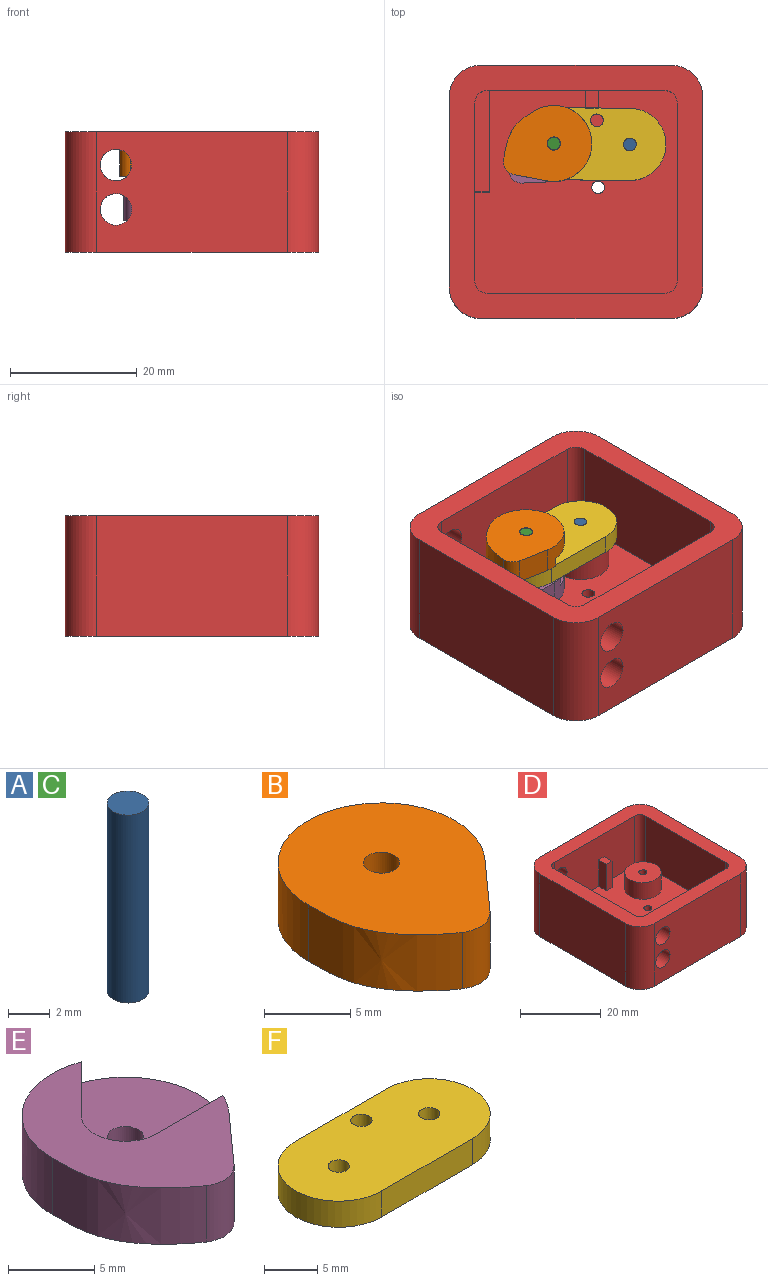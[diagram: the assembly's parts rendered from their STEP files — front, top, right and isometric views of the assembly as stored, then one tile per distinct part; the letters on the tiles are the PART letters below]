
ASSEMBLY  parts=6 mates=10
PART A: 3 faces, bbox 2x2x11 mm
  f0: cylinder r=1mm len=11mm, axis (0,0,-1), area 69.1mm2, adj f1,f2
  f1: plane 2x2mm, normal (0,0,1), area 3.1mm2, adj f0
  f2: plane 2x2mm, normal (0,0,-1), area 3.1mm2, adj f0
PART B: 11 faces, bbox 12.1x14.6x4 mm
  f0: cylinder r=6mm len=12mm, axis (0,0,-1), area 77.9mm2, adj f1,f2,f5,f6,f7,f8,f9
  f1: plane 4x3.93mm, normal (0.75,-0.67,0), area 21.1mm2, adj f0,f4,f5,f6
  f2: extruded ~8.25x4.36mm, area 39.4mm2, adj f0,f4,f5,f6
  f3: cylinder r=1.05mm len=2.5mm, axis (0,0,-1), area 16.5mm2, adj f5,f7
  f4: cylinder r=2mm len=4mm, axis (0,0,-1), area 11.5mm2, adj f1,f2,f5,f6
  f5: plane 14.59x12.11mm, normal (0,0,1), area 126.6mm2, adj f0,f1,f2,f3,f4
  f6: plane 14.59x11.54mm, normal (0,0,-1), area 78.6mm2, adj f0,f1,f2,f4,f8,f9,f10
  f7: plane 8.55x8.19mm, normal (0,0,-1), area 48mm2, adj f0,f3,f8,f9,f10
  f8: plane 5.43x1.5mm, normal (0,1,0), area 8.1mm2, adj f0,f6,f7,f10
  f9: plane 3.84x3.84mm, normal (0.71,-0.71,0), area 8.1mm2, adj f0,f6,f7,f10
  f10: cylinder r=2.55mm len=4.35mm, axis (0,0,-1), area 9mm2, adj f6,f7,f8,f9
PART C: same geometry as A
PART D: 36 faces, bbox 40x40x19 mm
  f0: plane 32x32mm, normal (0,0,1), area 911.9mm2, adj f1,f3,f14,f15,f16,f17,f18,f19
  f1: plane 28x15mm, normal (1,0,0), area 257mm2, adj f0,f2,f12,f14,f31,f35
  f2: cylinder r=2mm len=3.35mm, axis (0,0,1), area 10.5mm2, adj f1,f3,f12,f31
  f3: plane 28x15mm, normal (0,-1,0), area 365.2mm2, adj f0,f2,f12,f18,f22,f24,f25,f27
  f4: plane 30x19mm, normal (1,0,0), area 570mm2, adj f5,f11,f12,f13
  f5: cylinder r=5mm len=19mm, axis (0,0,-1), area 149.2mm2, adj f4,f6,f12,f13
  f6: plane 30x19mm, normal (0,1,0), area 530.7mm2, adj f5,f7,f12,f13,f27,f28
  f7: cylinder r=5mm len=19mm, axis (0,0,-1), area 149.2mm2, adj f6,f8,f12,f13
  f8: plane 30x19mm, normal (-1,0,0), area 570mm2, adj f7,f9,f12,f13
  f9: cylinder r=5mm len=19mm, axis (0,0,-1), area 149.2mm2, adj f8,f10,f12,f13
  f10: plane 30x19mm, normal (0,-1,0), area 530.7mm2, adj f9,f11,f12,f13,f29,f30
  f11: cylinder r=5mm len=19mm, axis (0,0,-1), area 149.2mm2, adj f4,f10,f12,f13
  f12: plane 40x40mm, normal (0,0,1), area 558mm2, adj f1,f2,f3,f4,f5,f6,f7,f8
  f13: plane 40x40mm, normal (0,0,-1), area 1572.3mm2, adj f4,f5,f6,f7,f8,f9,f10,f11
  f14: cylinder r=2mm len=15mm, axis (0,0,1), area 45.1mm2, adj f0,f1,f12,f15,f29,f30
  f15: plane 28x15mm, normal (0,1,0), area 382.8mm2, adj f0,f12,f14,f16,f29,f30
  f16: cylinder r=2mm len=15mm, axis (0,0,1), area 47.1mm2, adj f0,f12,f15,f17
  f17: plane 28x15mm, normal (-1,0,0), area 420mm2, adj f0,f12,f16,f18
  f18: cylinder r=2mm len=15mm, axis (0,0,1), area 47.1mm2, adj f0,f3,f12,f17
  f19: cylinder r=4.5mm len=9mm, axis (0,0,-1), area 141.4mm2, adj f0,f20
  f20: plane 9x9mm, normal (0,0,1), area 60.5mm2, adj f19,f21
  f21: cylinder r=1mm len=9mm, axis (0,0,1), area 56.5mm2, adj f13,f20
  f22: plane 8x2.75mm, normal (-1,0,0), area 22mm2, adj f0,f3,f23,f25
  f23: plane 8x2mm, normal (0,-1,0), area 16mm2, adj f0,f22,f24,f25
  f24: plane 8x2.75mm, normal (1,0,0), area 22mm2, adj f0,f3,f23,f25
  f25: plane 2.75x2mm, normal (0,0,1), area 5.5mm2, adj f3,f22,f23,f24
  f26: cylinder r=1mm len=4mm, axis (0,0,1), area 25.1mm2, adj f0,f13
  f27: cylinder r=2.5mm len=20mm, axis (0,-1,0), area 130mm2, adj f3,f6,f32,f33,f35
  f28: cylinder r=2.5mm len=20mm, axis (0,-1,0), area 130mm2, adj f3,f6,f33,f34,f35
  f29: cylinder r=2.5mm len=5mm, axis (0,-1,0), area 62.9mm2, adj f10,f14,f15
  f30: cylinder r=2.5mm len=5mm, axis (0,-1,0), area 62.9mm2, adj f10,f14,f15
  f31: plane 16x2.33mm, normal (0,0,1), area 36.4mm2, adj f1,f2,f3,f34,f35
  f32: plane 16x0.89mm, normal (1,0,0), area 14.2mm2, adj f0,f3,f27,f35
  f33: plane 16x3.28mm, normal (1,0,0), area 52.5mm2, adj f3,f27,f28,f35
  f34: plane 16x0.04mm, normal (1,0,0), area 0.6mm2, adj f3,f28,f31,f35
  f35: plane 11.65x2.33mm, normal (0,-1,0), area 22.9mm2, adj f0,f1,f27,f28,f31,f32,f33,f34
PART E: 11 faces, bbox 12.1x14.6x4 mm
  f0: cylinder r=1.05mm len=2.5mm, axis (0,0,1), area 16.5mm2, adj f5,f10
  f1: plane 4x3.93mm, normal (0.75,-0.67,0), area 21.1mm2, adj f2,f4,f5,f6
  f2: cylinder r=6mm len=12mm, axis (0,0,1), area 77.9mm2, adj f1,f3,f5,f6,f7,f8,f10
  f3: extruded ~8.25x4.36mm, area 39.4mm2, adj f2,f4,f5,f6
  f4: cylinder r=2mm len=4mm, axis (0,0,1), area 11.5mm2, adj f1,f3,f5,f6
  f5: plane 14.59x12.11mm, normal (0,0,-1), area 126.6mm2, adj f0,f1,f2,f3,f4
  f6: plane 14.59x11.54mm, normal (0,0,1), area 78.6mm2, adj f1,f2,f3,f4,f7,f8,f9
  f7: plane 5.43x1.5mm, normal (0,1,0), area 8.1mm2, adj f2,f6,f9,f10
  f8: plane 3.84x3.84mm, normal (0.71,-0.71,0), area 8.1mm2, adj f2,f6,f9,f10
  f9: cylinder r=2.55mm len=4.35mm, axis (0,0,1), area 9mm2, adj f6,f7,f8,f10
  f10: plane 8.55x8.19mm, normal (0,0,1), area 48mm2, adj f0,f2,f7,f8,f9
PART F: 9 faces, bbox 23.4x11.4x3 mm
  f0: plane 12x3mm, normal (0,1,0), area 36mm2, adj f1,f5,f7,f8
  f1: cylinder r=5.7mm len=11.4mm, axis (0,0,-1), area 53.7mm2, adj f0,f2,f7,f8
  f2: plane 12x3mm, normal (0,-1,0), area 36mm2, adj f1,f5,f7,f8
  f3: cylinder r=1mm len=3mm, axis (0,0,-1), area 18.8mm2, adj f7,f8
  f4: cylinder r=1mm len=3mm, axis (0,0,-1), area 18.8mm2, adj f7,f8
  f5: cylinder r=5.7mm len=11.4mm, axis (0,0,-1), area 53.7mm2, adj f0,f2,f7,f8
  f6: cylinder r=1mm len=3mm, axis (0,0,-1), area 18.8mm2, adj f7,f8
  f7: plane 23.4x11.4mm, normal (0,0,1), area 229.4mm2, adj f0,f1,f2,f3,f4,f5,f6
  f8: plane 23.4x11.4mm, normal (0,0,-1), area 229.4mm2, adj f0,f1,f2,f3,f4,f5,f6
PLACE A rot(axis=(0,0,1),15.9deg) t=(1.3,-5.21,5.99)mm
PLACE B rot(axis=(0,0,-1),58.9deg) t=(-10.7,-5.06,11.49)mm
PLACE C rot(axis=(0,0,1),41.8deg) t=(-10.7,-5.06,9.99)mm
PLACE D rot(axis=(0,0,1),0deg) t=(-7.2,-12.71,-0.51)mm fixed
PLACE E rot(axis=(0,0,-1),45.6deg) t=(-10.7,-5.06,8.49)mm
PLACE F rot(axis=(0,0,-1),0.7deg) t=(-10.7,-5.06,9.99)mm
MATE cylindrical C.f0 <-> E.f0  axis (0,0,-1) through (-10.7,-5.06,9.99)mm
MATE planar C.f0 <-> B.f5  axis (0,0,1) through (-10.7,-5.06,15.49)mm
MATE cylindrical A.f0 <-> F.f3  axis (0,0,-1) through (1.3,-5.21,5.99)mm
MATE planar F.f7 <-> A.f0  axis (0,0,1) through (-4.71,-5.18,11.49)mm
MATE cylindrical C.f0 <-> B.f3  axis (0,0,-1) through (-10.7,-5.06,15.49)mm
MATE cylindrical A.f0 <-> D.f19  axis (0,0,-1) through (1.3,-5.21,11.49)mm
MATE cylindrical F.f4 <-> C.f0  axis (0,0,-1) through (-10.7,-5.06,9.99)mm
MATE planar F.f8 <-> E.f4  axis (0,0,-1) through (-4.71,-5.18,8.49)mm
MATE planar F.f7 <-> B.f4  axis (0,0,1) through (-4.71,-5.18,11.49)mm
MATE planar F.f8 <-> D.f19  axis (0,0,-1) through (-4.71,-5.18,8.49)mm
